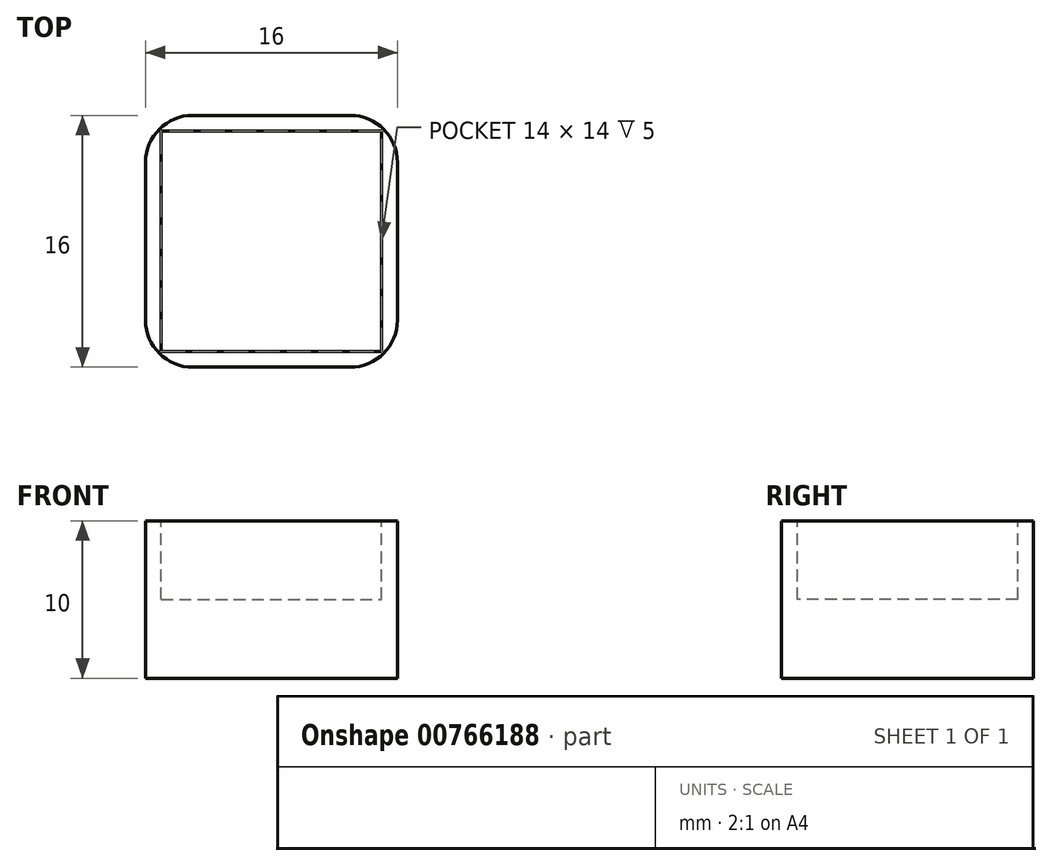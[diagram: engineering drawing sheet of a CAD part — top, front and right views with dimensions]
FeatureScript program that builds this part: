
annotation { "Feature Type Name" : "Feature", "Feature Type Description" : "" }
export const myFeature = defineFeature(function(context is Context, id is Id, definition is map)
    precondition{}
    {
        {
            var Q0;
            Q0=qCreatedBy(makeId("Top.planeOp"),FACE);
            var sketch = newSketch(context, id + "F0", { "sketchPlane" : qUnion([Q0])});
            skLineSegment(sketch, "E0.bottom", {"start": v(-8, 8) * mm, "end": v(8, 8) * mm});
            skLineSegment(sketch, "E0.top", {"start": v(-8, -8) * mm, "end": v(8, -8) * mm});
            skLineSegment(sketch, "E0.left", {"start": v(-8, 8) * mm, "end": v(-8, -8) * mm});
            skLineSegment(sketch, "E0.right", {"start": v(8, 8) * mm, "end": v(8, -8) * mm});
            skPoint(sketch, "E0.middle", {"position": v(0, 0) * mm});
            skSolve(sketch);
        }
        {
            var Q0;
            Q0=makeQuery(id+"F0.imprint","IMPRINT",FACE,{"disambiguationData":[TD([[makeQuery(id+"F0.imprint","IMPRINT",EDGE,{"derivedFrom":sQuery(id+"F0.wireOp",EDGE,"E0.bottom")}),-1.0]])]});
            extrude(context, id + "F1", {"entities" : qUnion([Q0]), "depth" : 10 * mm, "offsetDistance" : 25 * mm});
        }
        {
            var Q0;
            Q0=makeQuery(id+"F1.opExtrude","CAP_FACE",FACE,{"disambiguationData":[OSD([sQuery(id+"F0.wireOp",EDGE,"E0.bottom"),sQuery(id+"F0.wireOp",EDGE,"E0.top"),sQuery(id+"F0.wireOp",EDGE,"E0.left"),sQuery(id+"F0.wireOp",EDGE,"E0.right")])],"isStart":false});
            var sketch = newSketch(context, id + "F2", { "sketchPlane" : qUnion([Q0])});
            skLineSegment(sketch, "E1.bottom", {"start": v(-7, 7) * mm, "end": v(7, 7) * mm});
            skLineSegment(sketch, "E1.top", {"start": v(-7, -7) * mm, "end": v(7, -7) * mm});
            skLineSegment(sketch, "E1.left", {"start": v(-7, 7) * mm, "end": v(-7, -7) * mm});
            skLineSegment(sketch, "E1.right", {"start": v(7, 7) * mm, "end": v(7, -7) * mm});
            skPoint(sketch, "E1.middle", {"position": v(0, 0) * mm});
            skSolve(sketch);
        }
        {
            var Q0;
            Q0=makeQuery(id+"F2.imprint","IMPRINT",FACE,{"disambiguationData":[TD([[makeQuery(id+"F2.imprint","IMPRINT",EDGE,{"derivedFrom":sQuery(id+"F2.wireOp",EDGE,"E1.bottom")}),-1.0]])]});
            extrude(context, id + "F3", {"entities" : qUnion([Q0]), "operationType" : NewBodyOperationType.REMOVE, "oppositeDirection" : true, "depth" : 5 * mm, "offsetDistance" : 25 * mm});
        }
        {
            var Q0;
            Q0=makeQuery(id+"F3.opExtrude","SWEPT_EDGE",EDGE,{"disambiguationData":[OSD([sQuery(id+"F2.wireOp",EDGE,"E1.top"),sQuery(id+"F2.wireOp",EDGE,"E1.right")])]});
            var Q1;
            Q1=makeQuery(id+"F3.opExtrude","SWEPT_EDGE",EDGE,{"disambiguationData":[OSD([sQuery(id+"F2.wireOp",EDGE,"E1.bottom"),sQuery(id+"F2.wireOp",EDGE,"E1.right")])]});
            var Q2;
            Q2=makeQuery(id+"F3.opExtrude","SWEPT_EDGE",EDGE,{"disambiguationData":[OSD([sQuery(id+"F2.wireOp",EDGE,"E1.top"),sQuery(id+"F2.wireOp",EDGE,"E1.left")])]});
            var Q3;
            Q3=makeQuery(id+"F1.opExtrude","SWEPT_EDGE",EDGE,{"disambiguationData":[OSD([sQuery(id+"F0.wireOp",EDGE,"E0.top"),sQuery(id+"F0.wireOp",EDGE,"E0.left")])]});
            var Q4;
            Q4=makeQuery(id+"F1.opExtrude","SWEPT_EDGE",EDGE,{"disambiguationData":[OSD([sQuery(id+"F0.wireOp",EDGE,"E0.top"),sQuery(id+"F0.wireOp",EDGE,"E0.right")])]});
            var Q5;
            Q5=makeQuery(id+"F1.opExtrude","SWEPT_EDGE",EDGE,{"disambiguationData":[OSD([sQuery(id+"F0.wireOp",EDGE,"E0.bottom"),sQuery(id+"F0.wireOp",EDGE,"E0.right")])]});
            var Q6;
            Q6=makeQuery(id+"F1.opExtrude","SWEPT_EDGE",EDGE,{"disambiguationData":[OSD([sQuery(id+"F0.wireOp",EDGE,"E0.bottom"),sQuery(id+"F0.wireOp",EDGE,"E0.left")])]});
            var Q7;
            Q7=makeQuery(id+"F3.opExtrude","SWEPT_EDGE",EDGE,{"disambiguationData":[OSD([sQuery(id+"F2.wireOp",EDGE,"E1.bottom"),sQuery(id+"F2.wireOp",EDGE,"E1.left")])]});
            fillet(context, id + "F4", {"entities" : qUnion([Q0, Q1, Q2, Q3, Q4, Q5, Q6, Q7]), "radius" : 3 * mm, "tangentPropagation" : true, "allowEdgeOverflow" : false});
        }
    });
